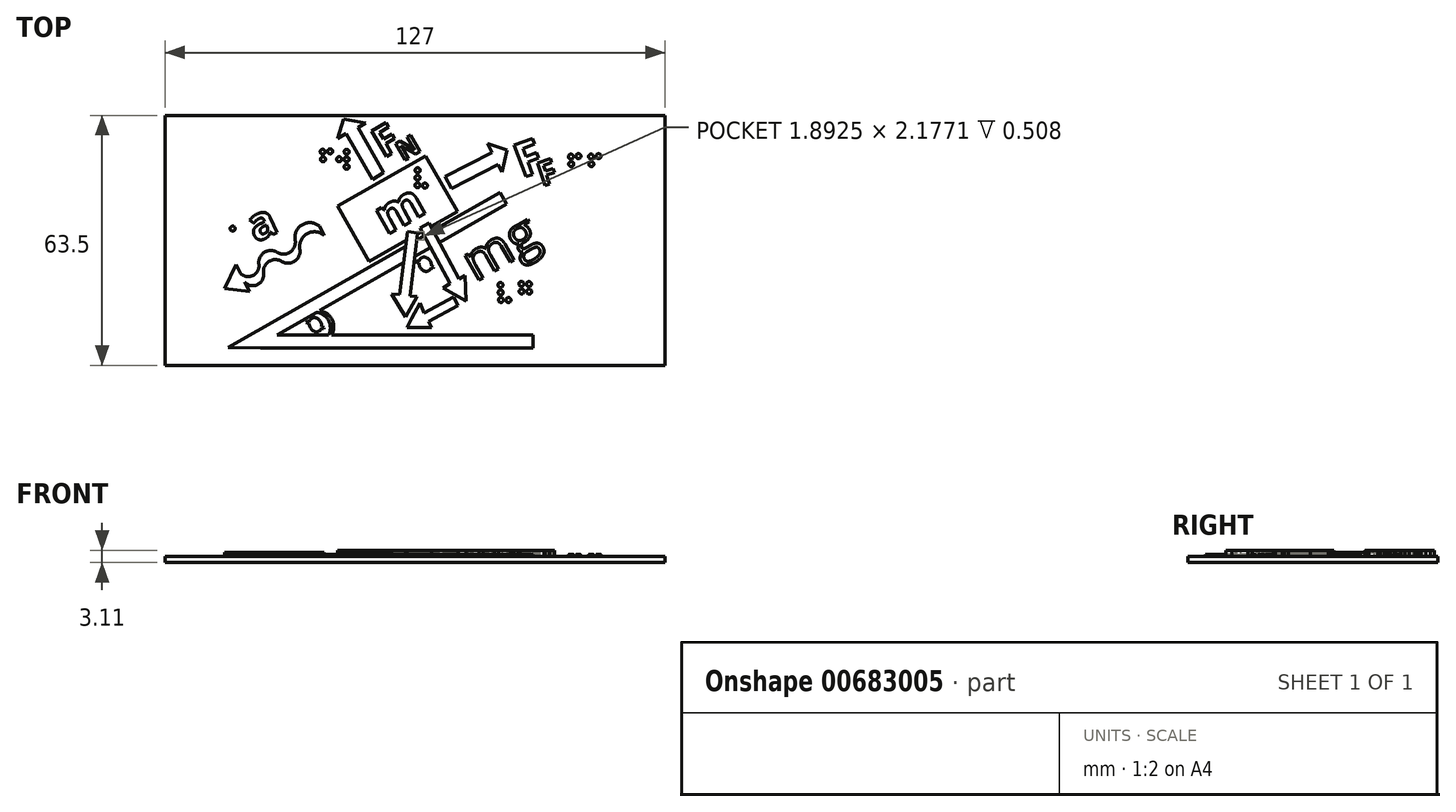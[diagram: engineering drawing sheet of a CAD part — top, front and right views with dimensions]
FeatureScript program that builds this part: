
annotation { "Feature Type Name" : "Feature", "Feature Type Description" : "" }
export const myFeature = defineFeature(function(context is Context, id is Id, definition is map)
    precondition{}
    {
        {
            var Q0;
            Q0=qCreatedBy(makeId("Top.planeOp"),FACE);
            var sketch = newSketch(context, id + "F0", { "sketchPlane" : qUnion([Q0])});
            skLineSegment(sketch, "E0.bottom", {"start": v(0, 0) * mm, "end": v(127, 0) * mm});
            skLineSegment(sketch, "E0.top", {"start": v(0, 63.5) * mm, "end": v(127, 63.5) * mm});
            skLineSegment(sketch, "E0.left", {"start": v(0, 0) * mm, "end": v(0, 63.5) * mm});
            skLineSegment(sketch, "E0.right", {"start": v(127, 0) * mm, "end": v(127, 63.5) * mm});
            skSolve(sketch);
        }
        {
            var Q0;
            Q0=makeQuery(id+"F0.imprint","IMPRINT",FACE,{"disambiguationData":[TD([[makeQuery(id+"F0.imprint","IMPRINT",EDGE,{"derivedFrom":sQuery(id+"F0.wireOp",EDGE,"E0.bottom")}),1.0]])]});
            extrude(context, id + "F1", {"entities" : qUnion([Q0]), "depth" : 1.59 * mm, "offsetDistance" : 25.4 * mm});
        }
        {
            var Q0;
            {var subQ0=sQuery(id+"F0.wireOp",EDGE,"E0.left");var subQ2=sQuery(id+"F0.wireOp",EDGE,"E0.top");var subQ4=sQuery(id+"F0.wireOp",EDGE,"E0.bottom");var subQ5=makeQuery(id+"F1.opExtrude","SWEPT_FACE",FACE,{"disambiguationData":[OSD([subQ4])]});var subQ9=sQuery(id+"F0.wireOp",EDGE,"E0.right");Q0=makeQuery(id+"F7.boolean.opBoolean","SPLIT",FACE,{"disambiguationData":[TD([subQ5])],"derivedFrom":makeQuery(id+"F5.boolean.opBoolean","SPLIT",FACE,{"disambiguationData":[TD([subQ5])],"derivedFrom":makeQuery(id+"F1.opExtrude","CAP_FACE",FACE,{"disambiguationData":[OSD([subQ4,subQ2,subQ0,subQ9])],"isStart":false})})});}
            var sketch = newSketch(context, id + "F2", { "sketchPlane" : qUnion([Q0])});
            skLineSegment(sketch, "E1", {"start": v(52.68, 47.22) * mm, "end": v(46.03, 58.88) * mm});
            skLineSegment(sketch, "E2", {"start": v(46.03, 58.88) * mm, "end": v(43.83, 57.63) * mm});
            skLineSegment(sketch, "E3", {"start": v(50.93, 61.6) * mm, "end": v(49.03, 60.45) * mm});
            skLineSegment(sketch, "E4", {"start": v(49.03, 60.45) * mm, "end": v(55.56, 48.98) * mm});
            skLineSegment(sketch, "E5", {"start": v(55.56, 48.98) * mm, "end": v(52.68, 47.22) * mm});
            skLineSegment(sketch, "E6", {"start": v(45.31, 62.57) * mm, "end": v(50.93, 61.6) * mm});
            skLineSegment(sketch, "E7", {"start": v(43.83, 57.63) * mm, "end": v(45.31, 62.57) * mm});
            skLineSegment(sketch, "E8", {"start": v(71.2, 47.9) * mm, "end": v(83.12, 54.07) * mm});
            skLineSegment(sketch, "E9", {"start": v(83.12, 54.07) * mm, "end": v(81.96, 56.33) * mm});
            skLineSegment(sketch, "E10", {"start": v(85.63, 49.07) * mm, "end": v(84.56, 51.01) * mm});
            skLineSegment(sketch, "E11", {"start": v(84.56, 51.01) * mm, "end": v(72.84, 44.95) * mm});
            skLineSegment(sketch, "E12", {"start": v(72.84, 44.95) * mm, "end": v(71.2, 47.9) * mm});
            skLineSegment(sketch, "E13", {"start": v(86.83, 54.64) * mm, "end": v(85.63, 49.07) * mm});
            skLineSegment(sketch, "E14", {"start": v(81.96, 56.33) * mm, "end": v(86.83, 54.64) * mm});
            skLineSegment(sketch, "E15", {"start": v(67.09, 36.17) * mm, "end": v(74.65, 21.92) * mm});
            skLineSegment(sketch, "E16", {"start": v(74.65, 21.92) * mm, "end": v(76.24, 22.77) * mm});
            skLineSegment(sketch, "E17", {"start": v(70.64, 19.62) * mm, "end": v(72.34, 20.73) * mm});
            skLineSegment(sketch, "E18", {"start": v(72.34, 20.73) * mm, "end": v(64.79, 34.9) * mm});
            skLineSegment(sketch, "E19", {"start": v(64.79, 34.9) * mm, "end": v(67.09, 36.17) * mm});
            skLineSegment(sketch, "E20", {"start": v(76.43, 16.38) * mm, "end": v(70.64, 19.62) * mm});
            skLineSegment(sketch, "E21", {"start": v(76.24, 22.77) * mm, "end": v(76.43, 16.38) * mm});
            skLineSegment(sketch, "E22", {"start": v(64.19, 33.65) * mm, "end": v(62.2, 17.65) * mm});
            skLineSegment(sketch, "E23", {"start": v(62.2, 17.65) * mm, "end": v(64, 17.42) * mm});
            skLineSegment(sketch, "E24", {"start": v(57.6, 18.06) * mm, "end": v(59.64, 17.99) * mm});
            skLineSegment(sketch, "E25", {"start": v(59.64, 17.99) * mm, "end": v(61.57, 33.93) * mm});
            skLineSegment(sketch, "E26", {"start": v(61.57, 33.93) * mm, "end": v(64.19, 33.65) * mm});
            skLineSegment(sketch, "E27", {"start": v(61.17, 12.24) * mm, "end": v(57.6, 18.06) * mm});
            skLineSegment(sketch, "E28", {"start": v(64, 17.42) * mm, "end": v(61.17, 12.24) * mm});
            skLineSegment(sketch, "E29", {"start": v(62.59, 11.93) * mm, "end": v(64.74, 15.88) * mm});
            skPoint(sketch, "E29.startSnap0", {"position": v(62.59, 14.83) * mm});
            skLineSegment(sketch, "E30", {"start": v(64.74, 15.88) * mm, "end": v(65.77, 13.33) * mm});
            skLineSegment(sketch, "E31", {"start": v(65.77, 13.33) * mm, "end": v(73.24, 17.35) * mm});
            skLineSegment(sketch, "E32", {"start": v(73.24, 17.35) * mm, "end": v(74.41, 15.16) * mm});
            skLineSegment(sketch, "E33", {"start": v(74.41, 15.16) * mm, "end": v(66.91, 11.12) * mm});
            skLineSegment(sketch, "E34", {"start": v(66.91, 11.12) * mm, "end": v(67.7, 9.65) * mm});
            skLineSegment(sketch, "E35", {"start": v(67.7, 9.65) * mm, "end": v(61.5, 9.65) * mm});
            skLineSegment(sketch, "E36", {"start": v(61.5, 9.65) * mm, "end": v(62.59, 11.93) * mm});
            skText(sketch, "E37", { "text": "F", "fontName": "OpenSans-Bold.ttf"});
            skText(sketch, "E38", { "text": "N", "fontName": "OpenSans-Bold.ttf"});
            skText(sketch, "E39", { "text": "F", "fontName": "OpenSans-Bold.ttf"});
            skText(sketch, "E40", { "text": "F", "fontName": "OpenSans-Bold.ttf"});
            skText(sketch, "E41", { "text": "mg", "fontName": "OpenSans-Regular.ttf"});
            skEllipticalArc(sketch, "E42", {});
            skFitSpline(sketch, "E43.0", {"points": [v(65.8, 27.08) * mm, v(65.41, 27) * mm, v(65.12, 26.74) * mm, v(64.93, 26.3) * mm, v(64.92, 25.75) * mm, v(65.1, 25.16) * mm, v(65.47, 24.67) * mm, v(65.93, 24.35) * mm, v(66.4, 24.25) * mm, v(66.77, 24.35) * mm, v(67.07, 24.6) * mm, v(67.26, 25.03) * mm, v(67.27, 25.6) * mm, v(67.08, 26.18) * mm, v(66.72, 26.67) * mm, v(66.25, 26.99) * mm, v(65.8, 27.08) * mm, v(65.41, 27) * mm, v(65.12, 26.74) * mm]});
            skLineSegment(sketch, "E44", {"start": v(63.77, 26.22) * mm, "end": v(64.5, 25.95) * mm});
            skLineSegment(sketch, "E45", {"start": v(68.11, 24.62) * mm, "end": v(68.25, 24.98) * mm});
            skLineSegment(sketch, "E46", {"start": v(68.25, 24.98) * mm, "end": v(67.68, 25.19) * mm});
            skLineSegment(sketch, "E47", {"start": v(63.94, 26.56) * mm, "end": v(63.77, 26.22) * mm});
            skFitSpline(sketch, "E48.trimOffspring", {"points": [v(65.8, 27.08) * mm, v(65.41, 27) * mm, v(65.12, 26.74) * mm, v(64.93, 26.3) * mm, v(64.92, 25.75) * mm, v(65.1, 25.16) * mm, v(65.47, 24.67) * mm, v(65.93, 24.35) * mm, v(66.4, 24.25) * mm, v(66.77, 24.35) * mm, v(67.07, 24.6) * mm, v(67.26, 25.03) * mm, v(67.27, 25.6) * mm, v(67.08, 26.18) * mm, v(66.72, 26.67) * mm, v(66.25, 26.99) * mm, v(65.8, 27.08) * mm, v(65.41, 27) * mm, v(65.12, 26.74) * mm]});
            skEllipticalArc(sketch, "E49.trimOffspring", {});
            skLineSegment(sketch, "E50.trimOffspring", {"start": v(67.61, 24.8) * mm, "end": v(68.11, 24.62) * mm});
            skLineSegment(sketch, "E51.trimOffspring", {"start": v(67.26, 25.34) * mm, "end": v(64.94, 26.2) * mm});
            skLineSegment(sketch, "E52.trimOffspring", {"start": v(64.53, 26.35) * mm, "end": v(63.94, 26.56) * mm});
            skLineSegment(sketch, "E53", {"start": v(64.94, 25.79) * mm, "end": v(67.2, 24.96) * mm});
            const initialGuessF2  = {"E37": [0.05542, 0.05258, 0.86603, 0.5, 0.0075], "E38": [0.0605, 0.05183, 0.86603, 0.5, 0.00486], "E39": [0.09064, 0.04753, 0.9397, 0.34202, 0.0086], "E40": [0.09575, 0.04539, 0.9518, 0.30672, 0.00612], "E41": [0.07882, 0.0211, 0.86603, 0.5, 0.00963], "E42": [0.06609338407474807, 0.025668868562019675, -0.4576420160499878, 0.8891365390904272, 0.0018890030002759763, 0.0015080474726828794, 1.0254476963977666, 3.8274184167815006], "E49.trimOffspring": [0.06609338407474807, 0.025668868562019675, -0.4576420160499878, 0.8891365390904272, 0.0018890030002759763, 0.0015080474726828794, 4.0541978294457675, 0.7986682837335095]};
            skSetInitialGuess(sketch, initialGuessF2);
            skSolve(sketch);
        }
        {
            var Q0;
            Q0=makeQuery(id+"F2.imprint","IMPRINT",FACE,{"disambiguationData":[TD([[makeQuery(id+"F2.imprint","IMPRINT",EDGE,{"derivedFrom":sQuery(id+"F2.wireOp",EDGE,"E37.sketch_text.stroke-0")}),-1.0]])]});
            var Q1;
            Q1=makeQuery(id+"F2.imprint","IMPRINT",FACE,{"disambiguationData":[TD([[makeQuery(id+"F2.imprint","IMPRINT",EDGE,{"derivedFrom":sQuery(id+"F2.wireOp",EDGE,"E38.sketch_text.stroke-0")}),-1.0]])]});
            var Q2;
            Q2=makeQuery(id+"F2.imprint","IMPRINT",FACE,{"disambiguationData":[TD([[makeQuery(id+"F2.imprint","IMPRINT",EDGE,{"derivedFrom":sQuery(id+"F2.wireOp",EDGE,"E39.sketch_text.stroke-0")}),-1.0]])]});
            var Q3;
            Q3=makeQuery(id+"F2.imprint","IMPRINT",FACE,{"disambiguationData":[TD([[makeQuery(id+"F2.imprint","IMPRINT",EDGE,{"derivedFrom":sQuery(id+"F2.wireOp",EDGE,"E40.sketch_text.stroke-0")}),-1.0]])]});
            var Q4;
            Q4=makeQuery(id+"F2.imprint","IMPRINT",FACE,{"disambiguationData":[TD([[makeQuery(id+"F2.imprint","IMPRINT",EDGE,{"derivedFrom":sQuery(id+"F2.wireOp",EDGE,"E41.sketch_text.stroke-28")}),-1.0]])]});
            var Q5;
            Q5=makeQuery(id+"F2.imprint","IMPRINT",FACE,{"disambiguationData":[TD([[makeQuery(id+"F2.imprint","IMPRINT",EDGE,{"derivedFrom":sQuery(id+"F2.wireOp",EDGE,"E41.sketch_text.stroke-0")}),-1.0]])]});
            var Q6;
            Q6=makeQuery(id+"F2.imprint","IMPRINT",FACE,{"disambiguationData":[TD([[makeQuery(id+"F2.imprint","IMPRINT",EDGE,{"derivedFrom":sQuery(id+"F2.wireOp",EDGE,"E42")}),1.0]])]});
            var Q7;
            {var subQ6=sQuery(id+"F2.wireOp",EDGE,"E23");Q7=makeQuery(id+"F2.imprint","IMPRINT",FACE,{"disambiguationData":[TD([[makeQuery(id+"F2.imprint","IMPRINT",EDGE,{"derivedFrom":subQ6}),-1.0]])]});}
            var Q8;
            Q8=makeQuery(id+"F2.imprint","IMPRINT",FACE,{"disambiguationData":[TD([[makeQuery(id+"F2.imprint","IMPRINT",EDGE,{"derivedFrom":sQuery(id+"F2.wireOp",EDGE,"E29")}),-1.0]])]});
            var Q9;
            {var subQ6=sQuery(id+"F2.wireOp",EDGE,"E16");Q9=makeQuery(id+"F2.imprint","IMPRINT",FACE,{"disambiguationData":[TD([[makeQuery(id+"F2.imprint","IMPRINT",EDGE,{"derivedFrom":subQ6}),-1.0]])]});}
            var Q10;
            {var subQ0=sQuery(id+"F2.wireOp",EDGE,"E22");var subQ1=makeQuery(id+"F7.opExtrude","CAP_EDGE",EDGE,{"disambiguationData":[OSD([sQuery(id+"F6.wireOp",EDGE,"E80")])],"isStart":true});var subQ2=makeQuery(id+"F2.imprint","INTERSECT",VERTEX,{"derivedFrom":[subQ1,subQ0]});Q10=makeQuery(id+"F2.imprint","IMPRINT",FACE,{"disambiguationData":[TD([[makeQuery(id+"F2.imprint","IMPRINT",EDGE,{"disambiguationData":[TD([[subQ2,-1.0]])],"derivedFrom":subQ0}),-1.0]])]});}
            var Q11;
            {var subQ0=sQuery(id+"F2.wireOp",EDGE,"E15");var subQ1=makeQuery(id+"F7.opExtrude","CAP_EDGE",EDGE,{"disambiguationData":[OSD([sQuery(id+"F6.wireOp",EDGE,"E80")])],"isStart":true});var subQ2=makeQuery(id+"F2.imprint","INTERSECT",VERTEX,{"derivedFrom":[subQ1,subQ0]});Q11=makeQuery(id+"F2.imprint","IMPRINT",FACE,{"disambiguationData":[TD([[makeQuery(id+"F2.imprint","IMPRINT",EDGE,{"disambiguationData":[TD([[subQ2,-1.0]])],"derivedFrom":subQ0}),-1.0]])]});}
            var Q12;
            Q12=makeQuery(id+"F2.imprint","IMPRINT",FACE,{"disambiguationData":[TD([[makeQuery(id+"F2.imprint","IMPRINT",EDGE,{"derivedFrom":sQuery(id+"F2.wireOp",EDGE,"E8")}),-1.0]])]});
            var Q13;
            Q13=makeQuery(id+"F2.imprint","IMPRINT",FACE,{"disambiguationData":[TD([[makeQuery(id+"F2.imprint","IMPRINT",EDGE,{"derivedFrom":sQuery(id+"F2.wireOp",EDGE,"E1")}),-1.0]])]});
            extrude(context, id + "F3", {"entities" : qUnion([Q0, Q1, Q2, Q3, Q4, Q5, Q6, Q7, Q8, Q9, Q10, Q11, Q12, Q13]), "operationType" : NewBodyOperationType.ADD, "depth" : 1.52 * mm, "offsetDistance" : 25.4 * mm});
        }
        {
            var Q0;
            Q0=makeQuery(id+"F1.opExtrude","CAP_FACE",FACE,{"disambiguationData":[OSD([sQuery(id+"F0.wireOp",EDGE,"E0.bottom"),sQuery(id+"F0.wireOp",EDGE,"E0.top"),sQuery(id+"F0.wireOp",EDGE,"E0.left"),sQuery(id+"F0.wireOp",EDGE,"E0.right")])],"isStart":false});
            var sketch = newSketch(context, id + "F4", { "sketchPlane" : qUnion([Q0])});
            skLineSegment(sketch, "E54", {"start": v(24.26, 4.4) * mm, "end": v(93.55, 4.4) * mm});
            skLineSegment(sketch, "E55", {"start": v(93.55, 4.4) * mm, "end": v(93.55, 7.72) * mm});
            skLineSegment(sketch, "E56", {"start": v(93.55, 7.72) * mm, "end": v(42.34, 7.72) * mm});
            skLineSegment(sketch, "E57", {"start": v(28.42, 7.72) * mm, "end": v(38.48, 13.46) * mm});
            skLineSegment(sketch, "E58", {"start": v(86.74, 40.95) * mm, "end": v(85.09, 43.85) * mm});
            skLineSegment(sketch, "E59", {"start": v(85.09, 43.85) * mm, "end": v(16.03, 4.5) * mm});
            skLineSegment(sketch, "E60", {"start": v(16.03, 4.5) * mm, "end": v(24.26, 4.4) * mm});
            skArc(sketch, "E61", {"start": v(41.55, 7.72) * mm, "mid": v(41.53, 11.4) * mm, "end": v(38.48, 13.46) * mm});
            skArc(sketch, "E62", {"start": v(42.34, 7.72) * mm, "mid": v(42.43, 11.63) * mm, "end": v(39.24, 13.89) * mm});
            skLineSegment(sketch, "E63.trimOffspring", {"start": v(39.24, 13.89) * mm, "end": v(86.74, 40.95) * mm});
            skLineSegment(sketch, "E64.trimOffspring", {"start": v(41.55, 7.72) * mm, "end": v(28.42, 7.72) * mm});
            skEllipticalArc(sketch, "E65", {});
            skFitSpline(sketch, "E66.0", {"points": [v(37.92, 11.73) * mm, v(37.54, 11.64) * mm, v(37.24, 11.39) * mm, v(37.05, 10.96) * mm, v(37.04, 10.4) * mm, v(37.23, 9.81) * mm, v(37.6, 9.32) * mm, v(38.06, 9) * mm, v(38.52, 8.9) * mm, v(38.9, 9) * mm, v(39.2, 9.25) * mm, v(39.38, 9.68) * mm, v(39.4, 10.24) * mm, v(39.2, 10.83) * mm, v(38.84, 11.32) * mm, v(38.38, 11.64) * mm, v(37.92, 11.73) * mm, v(37.54, 11.64) * mm, v(37.24, 11.39) * mm]});
            skLineSegment(sketch, "E67", {"start": v(35.9, 10.87) * mm, "end": v(36.62, 10.6) * mm});
            skLineSegment(sketch, "E68", {"start": v(40.24, 9.27) * mm, "end": v(40.37, 9.63) * mm});
            skLineSegment(sketch, "E69", {"start": v(40.37, 9.63) * mm, "end": v(39.8, 9.84) * mm});
            skLineSegment(sketch, "E70", {"start": v(36.06, 11.21) * mm, "end": v(35.9, 10.87) * mm});
            skFitSpline(sketch, "E71.trimOffspring", {"points": [v(37.92, 11.73) * mm, v(37.54, 11.64) * mm, v(37.24, 11.39) * mm, v(37.05, 10.96) * mm, v(37.04, 10.4) * mm, v(37.23, 9.81) * mm, v(37.6, 9.32) * mm, v(38.06, 9) * mm, v(38.52, 8.9) * mm, v(38.9, 9) * mm, v(39.2, 9.25) * mm, v(39.38, 9.68) * mm, v(39.4, 10.24) * mm, v(39.2, 10.83) * mm, v(38.84, 11.32) * mm, v(38.38, 11.64) * mm, v(37.92, 11.73) * mm, v(37.54, 11.64) * mm, v(37.24, 11.39) * mm]});
            skEllipticalArc(sketch, "E72.trimOffspring", {});
            skLineSegment(sketch, "E73.trimOffspring", {"start": v(39.74, 9.46) * mm, "end": v(40.24, 9.27) * mm});
            skLineSegment(sketch, "E74.trimOffspring", {"start": v(39.38, 10) * mm, "end": v(37.07, 10.84) * mm});
            skLineSegment(sketch, "E75.trimOffspring", {"start": v(36.65, 11) * mm, "end": v(36.06, 11.21) * mm});
            skLineSegment(sketch, "E76", {"start": v(37.07, 10.44) * mm, "end": v(39.33, 9.6) * mm});
            const initialGuessF4  = {"E65": [0.038218526944156374, 0.010319110858641223, -0.4576420160499878, 0.8891365390904272, 0.0018890030002759763, 0.0015080474726828794, 1.0254476963977666, 3.827418836985673], "E72.trimOffspring": [0.038218526944156374, 0.010319110858641223, -0.4576420160499878, 0.8891365390904272, 0.0018890030002759763, 0.0015080474726828794, 4.0541978294457675, 0.7986687039376736]};
            skSetInitialGuess(sketch, initialGuessF4);
            skSolve(sketch);
        }
        {
            var Q0;
            Q0=makeQuery(id+"F4.imprint","IMPRINT",FACE,{"disambiguationData":[TD([[makeQuery(id+"F4.imprint","IMPRINT",EDGE,{"derivedFrom":sQuery(id+"F4.wireOp",EDGE,"E54")}),1.0]])]});
            var Q1;
            Q1=makeQuery(id+"F4.imprint","IMPRINT",FACE,{"disambiguationData":[TD([[makeQuery(id+"F4.imprint","IMPRINT",EDGE,{"derivedFrom":sQuery(id+"F4.wireOp",EDGE,"E65")}),1.0]])]});
            var Q2;
            {var subQ0=sQuery(id+"F4.wireOp",EDGE,"E59");var subQ1=makeQuery(id+"F3.opExtrude","CAP_EDGE",EDGE,{"disambiguationData":[OSD([sQuery(id+"F2.wireOp",EDGE,"E18")])],"isStart":true});var subQ2=makeQuery(id+"F4.imprint","INTERSECT",VERTEX,{"derivedFrom":[subQ1,subQ0]});Q2=makeQuery(id+"F4.imprint","IMPRINT",FACE,{"disambiguationData":[TD([[makeQuery(id+"F4.imprint","IMPRINT",EDGE,{"disambiguationData":[TD([[subQ2,-1.0]])],"derivedFrom":subQ0}),1.0]])]});}
            var Q3;
            {var subQ0=sQuery(id+"F4.wireOp",EDGE,"E58");Q3=makeQuery(id+"F4.imprint","IMPRINT",FACE,{"disambiguationData":[TD([[makeQuery(id+"F4.imprint","IMPRINT",EDGE,{"derivedFrom":subQ0}),1.0]])]});}
            extrude(context, id + "F5", {"entities" : qUnion([Q0, Q1, Q2, Q3]), "operationType" : NewBodyOperationType.ADD, "depth" : 0.5 * mm, "offsetDistance" : 25.4 * mm});
        }
        {
            var Q0;
            {var subQ0=sQuery(id+"F0.wireOp",EDGE,"E0.left");var subQ1=sQuery(id+"F0.wireOp",EDGE,"E0.bottom");var subQ2=sQuery(id+"F0.wireOp",EDGE,"E0.right");var subQ3=sQuery(id+"F0.wireOp",EDGE,"E0.top");Q0=makeQuery(id+"F5.boolean.opBoolean","SPLIT",FACE,{"disambiguationData":[TD([makeQuery(id+"F1.opExtrude","SWEPT_FACE",FACE,{"disambiguationData":[OSD([subQ1])]})])],"derivedFrom":makeQuery(id+"F1.opExtrude","CAP_FACE",FACE,{"disambiguationData":[OSD([subQ1,subQ3,subQ0,subQ2])],"isStart":false})});}
            var sketch = newSketch(context, id + "F6", { "sketchPlane" : qUnion([Q0])});
            skLineSegment(sketch, "E77", {"start": v(51.82, 26.43) * mm, "end": v(43.83, 40.46) * mm});
            skLineSegment(sketch, "E78", {"start": v(43.83, 40.46) * mm, "end": v(66.23, 53.22) * mm});
            skLineSegment(sketch, "E79", {"start": v(66.23, 53.22) * mm, "end": v(74.3, 39.07) * mm});
            skLineSegment(sketch, "E80", {"start": v(74.3, 39.07) * mm, "end": v(51.82, 26.43) * mm});
            skText(sketch, "E81", { "text": "m", "fontName": "OpenSans-Bold.ttf"});
            skArc(sketch, "E82", {"start": v(40.42, 33.04) * mm, "mid": v(36.2, 33.5) * mm, "end": v(34.18, 29.79) * mm});
            skArc(sketch, "E83", {"start": v(29.81, 26.29) * mm, "mid": v(33.15, 26.6) * mm, "end": v(34.18, 29.79) * mm});
            skArc(sketch, "E84", {"start": v(29.81, 26.29) * mm, "mid": v(26.5, 26.44) * mm, "end": v(25, 23.49) * mm});
            skArc(sketch, "E85", {"start": v(20.18, 21.16) * mm, "mid": v(23.47, 20.5) * mm, "end": v(25, 23.49) * mm});
            skArc(sketch, "E86", {"start": v(39.23, 35.35) * mm, "mid": v(35.02, 35.82) * mm, "end": v(33, 32.1) * mm});
            skArc(sketch, "E87", {"start": v(28.63, 28.6) * mm, "mid": v(31.96, 28.91) * mm, "end": v(33, 32.1) * mm});
            skArc(sketch, "E88", {"start": v(28.63, 28.6) * mm, "mid": v(25.32, 28.75) * mm, "end": v(23.82, 25.8) * mm});
            skArc(sketch, "E89", {"start": v(19.19, 23.27) * mm, "mid": v(22.41, 22.87) * mm, "end": v(23.82, 25.8) * mm});
            skLineSegment(sketch, "E90", {"start": v(39.23, 35.35) * mm, "end": v(40.42, 33.04) * mm});
            skLineSegment(sketch, "E91", {"start": v(20.18, 21.16) * mm, "end": v(21.48, 18.77) * mm});
            skLineSegment(sketch, "E92", {"start": v(21.48, 18.77) * mm, "end": v(15.08, 19.55) * mm});
            skLineSegment(sketch, "E93", {"start": v(15.08, 19.55) * mm, "end": v(18.1, 25.57) * mm});
            skLineSegment(sketch, "E94", {"start": v(18.1, 25.57) * mm, "end": v(19.19, 23.27) * mm});
            skText(sketch, "E95", { "text": "a", "fontName": "OpenSans-Bold.ttf"});
            const initialGuessF6  = {"E81": [0.05625, 0.033, 0.87092, 0.49143, 0.00893], "E95": [0.023, 0.03117, 0.9063, 0.42262, 0.00829]};
            skSetInitialGuess(sketch, initialGuessF6);
            skSolve(sketch);
        }
        {
            var Q0;
            Q0=makeQuery(id+"F6.imprint","IMPRINT",FACE,{"disambiguationData":[TD([[makeQuery(id+"F6.imprint","IMPRINT",EDGE,{"derivedFrom":sQuery(id+"F6.wireOp",EDGE,"E82")}),-1.0]])]});
            var Q1;
            Q1=makeQuery(id+"F6.imprint","IMPRINT",FACE,{"disambiguationData":[TD([[makeQuery(id+"F6.imprint","IMPRINT",EDGE,{"derivedFrom":sQuery(id+"F6.wireOp",EDGE,"E95.sketch_text.stroke-0")}),-1.0]])]});
            var Q2;
            Q2=makeQuery(id+"F6.imprint","IMPRINT",FACE,{"disambiguationData":[TD([[makeQuery(id+"F6.imprint","IMPRINT",EDGE,{"derivedFrom":sQuery(id+"F6.wireOp",EDGE,"E77")}),-1.0]])]});
            extrude(context, id + "F7", {"entities" : qUnion([Q0, Q1, Q2]), "operationType" : NewBodyOperationType.ADD, "depth" : 1.02 * mm, "offsetDistance" : 25.4 * mm});
        }
        {
            var Q0;
            {var subQ19=sQuery(id+"F0.wireOp",EDGE,"E0.right");var subQ20=sQuery(id+"F0.wireOp",EDGE,"E0.left");var subQ21=sQuery(id+"F0.wireOp",EDGE,"E0.top");var subQ22=sQuery(id+"F0.wireOp",EDGE,"E0.bottom");var subQ23=makeQuery(id+"F1.opExtrude","CAP_FACE",FACE,{"disambiguationData":[OSD([subQ22,subQ21,subQ20,subQ19])],"isStart":false});var subQ86=makeQuery(id+"F1.opExtrude","SWEPT_FACE",FACE,{"disambiguationData":[OSD([subQ22])]});Q0=makeQuery(id+"F7.boolean.opBoolean","SPLIT",FACE,{"disambiguationData":[TD([subQ86])],"derivedFrom":makeQuery(id+"F5.boolean.opBoolean","SPLIT",FACE,{"disambiguationData":[TD([subQ86])],"derivedFrom":makeQuery(id+"F3.boolean.opBoolean","SPLIT",FACE,{"disambiguationData":[TD([subQ86])],"derivedFrom":subQ23})})});}
            var sketch = newSketch(context, id + "F8", { "sketchPlane" : qUnion([Q0])});
            skCircle(sketch, "E96", {"center": v(40.06, 54.25) * mm, "radius": 0.64 * mm});
            skCircle(sketch, "E97", {"center": v(41.96, 54.36) * mm, "radius": 0.64 * mm});
            skCircle(sketch, "E98", {"center": v(40.13, 52.34) * mm, "radius": 0.64 * mm});
            skCircle(sketch, "E99", {"center": v(44.23, 52.35) * mm, "radius": 0.64 * mm});
            skCircle(sketch, "E100", {"center": v(46.15, 54.24) * mm, "radius": 0.64 * mm});
            skCircle(sketch, "E101", {"center": v(46.13, 52.34) * mm, "radius": 0.64 * mm});
            skCircle(sketch, "E102", {"center": v(46.14, 50.43) * mm, "radius": 0.64 * mm});
            skCircle(sketch, "E103", {"center": v(103.13, 53.02) * mm, "radius": 0.64 * mm});
            skCircle(sketch, "E104", {"center": v(105.03, 53.14) * mm, "radius": 0.64 * mm});
            skCircle(sketch, "E105", {"center": v(103.2, 51.12) * mm, "radius": 0.64 * mm});
            skCircle(sketch, "E106", {"center": v(108.23, 53.03) * mm, "radius": 0.64 * mm});
            skCircle(sketch, "E107", {"center": v(110.13, 53.14) * mm, "radius": 0.64 * mm});
            skCircle(sketch, "E108", {"center": v(108.3, 51.12) * mm, "radius": 0.64 * mm});
            skCircle(sketch, "E109", {"center": v(85.22, 20.4) * mm, "radius": 0.64 * mm});
            skCircle(sketch, "E110", {"center": v(85.26, 18.5) * mm, "radius": 0.64 * mm});
            skCircle(sketch, "E111", {"center": v(85.34, 16.59) * mm, "radius": 0.64 * mm});
            skCircle(sketch, "E112", {"center": v(87.24, 16.58) * mm, "radius": 0.64 * mm});
            skCircle(sketch, "E113", {"center": v(90.55, 20.67) * mm, "radius": 0.64 * mm});
            skCircle(sketch, "E114", {"center": v(90.59, 18.76) * mm, "radius": 0.64 * mm});
            skCircle(sketch, "E115", {"center": v(92.45, 20.63) * mm, "radius": 0.64 * mm});
            skCircle(sketch, "E116", {"center": v(92.5, 18.72) * mm, "radius": 0.64 * mm});
            skCircle(sketch, "E117", {"center": v(17.17, 34.73) * mm, "radius": 0.64 * mm});
            skSolve(sketch);
        }
        {
            var Q0;
            Q0 = qSketchRegion(id + "F8", true);
            extrude(context, id + "F9", {"entities" : qUnion([Q0]), "operationType" : NewBodyOperationType.ADD, "depth" : 0.5 * mm, "offsetDistance" : 25.4 * mm});
        }
        {
            var Q0;
            Q0=makeQuery(id+"F9.opExtrude","CAP_EDGE",EDGE,{"disambiguationData":[OSD([sQuery(id+"F8.wireOp",EDGE,"E117")])],"isStart":false});
            var Q1;
            Q1=makeQuery(id+"F9.opExtrude","CAP_FACE",FACE,{"disambiguationData":[OSD([sQuery(id+"F8.wireOp",EDGE,"E98")])],"isStart":false});
            var Q2;
            Q2=makeQuery(id+"F9.opExtrude","CAP_EDGE",EDGE,{"disambiguationData":[OSD([sQuery(id+"F8.wireOp",EDGE,"E96")])],"isStart":false});
            var Q3;
            Q3=makeQuery(id+"F9.opExtrude","CAP_EDGE",EDGE,{"disambiguationData":[OSD([sQuery(id+"F8.wireOp",EDGE,"E97")])],"isStart":false});
            var Q4;
            Q4=makeQuery(id+"F9.opExtrude","CAP_EDGE",EDGE,{"disambiguationData":[OSD([sQuery(id+"F8.wireOp",EDGE,"E99")])],"isStart":false});
            var Q5;
            Q5=makeQuery(id+"F9.opExtrude","CAP_EDGE",EDGE,{"disambiguationData":[OSD([sQuery(id+"F8.wireOp",EDGE,"E101")])],"isStart":false});
            var Q6;
            Q6=makeQuery(id+"F9.opExtrude","CAP_EDGE",EDGE,{"disambiguationData":[OSD([sQuery(id+"F8.wireOp",EDGE,"E100")])],"isStart":false});
            var Q7;
            Q7=makeQuery(id+"F9.opExtrude","CAP_EDGE",EDGE,{"disambiguationData":[OSD([sQuery(id+"F8.wireOp",EDGE,"E102")])],"isStart":false});
            var Q8;
            Q8=makeQuery(id+"F9.opExtrude","CAP_EDGE",EDGE,{"disambiguationData":[OSD([sQuery(id+"F8.wireOp",EDGE,"E105")])],"isStart":false});
            var Q9;
            Q9=makeQuery(id+"F9.opExtrude","CAP_EDGE",EDGE,{"disambiguationData":[OSD([sQuery(id+"F8.wireOp",EDGE,"E103")])],"isStart":false});
            var Q10;
            Q10=makeQuery(id+"F9.opExtrude","CAP_EDGE",EDGE,{"disambiguationData":[OSD([sQuery(id+"F8.wireOp",EDGE,"E104")])],"isStart":false});
            var Q11;
            Q11=makeQuery(id+"F9.opExtrude","CAP_EDGE",EDGE,{"disambiguationData":[OSD([sQuery(id+"F8.wireOp",EDGE,"E106")])],"isStart":false});
            var Q12;
            Q12=makeQuery(id+"F9.opExtrude","CAP_EDGE",EDGE,{"disambiguationData":[OSD([sQuery(id+"F8.wireOp",EDGE,"E108")])],"isStart":false});
            var Q13;
            Q13=makeQuery(id+"F9.opExtrude","CAP_EDGE",EDGE,{"disambiguationData":[OSD([sQuery(id+"F8.wireOp",EDGE,"E107")])],"isStart":false});
            var Q14;
            Q14=makeQuery(id+"F9.opExtrude","CAP_EDGE",EDGE,{"disambiguationData":[OSD([sQuery(id+"F8.wireOp",EDGE,"E116")])],"isStart":false});
            var Q15;
            Q15=makeQuery(id+"F9.opExtrude","CAP_EDGE",EDGE,{"disambiguationData":[OSD([sQuery(id+"F8.wireOp",EDGE,"E115")])],"isStart":false});
            var Q16;
            Q16=makeQuery(id+"F9.opExtrude","CAP_EDGE",EDGE,{"disambiguationData":[OSD([sQuery(id+"F8.wireOp",EDGE,"E113")])],"isStart":false});
            var Q17;
            Q17=makeQuery(id+"F9.opExtrude","CAP_EDGE",EDGE,{"disambiguationData":[OSD([sQuery(id+"F8.wireOp",EDGE,"E114")])],"isStart":false});
            var Q18;
            Q18=makeQuery(id+"F9.opExtrude","CAP_EDGE",EDGE,{"disambiguationData":[OSD([sQuery(id+"F8.wireOp",EDGE,"E112")])],"isStart":false});
            var Q19;
            Q19=makeQuery(id+"F9.opExtrude","CAP_EDGE",EDGE,{"disambiguationData":[OSD([sQuery(id+"F8.wireOp",EDGE,"E111")])],"isStart":false});
            var Q20;
            Q20=makeQuery(id+"F9.opExtrude","CAP_EDGE",EDGE,{"disambiguationData":[OSD([sQuery(id+"F8.wireOp",EDGE,"E110")])],"isStart":false});
            var Q21;
            Q21=makeQuery(id+"F9.opExtrude","CAP_EDGE",EDGE,{"disambiguationData":[OSD([sQuery(id+"F8.wireOp",EDGE,"E109")])],"isStart":false});
            fillet(context, id + "F10", {"entities" : qUnion([Q0, Q1, Q2, Q3, Q4, Q5, Q6, Q7, Q8, Q9, Q10, Q11, Q12, Q13, Q14, Q15, Q16, Q17, Q18, Q19, Q20, Q21]), "radius" : 0.25 * mm, "tangentPropagation" : true, "allowEdgeOverflow" : false});
        }
        {
            var Q0;
            Q0=makeQuery(id+"F7.opExtrude","CAP_FACE",FACE,{"disambiguationData":[OSD([sQuery(id+"F2.wireOp",EDGE,"E15"),sQuery(id+"F2.wireOp",EDGE,"E18"),sQuery(id+"F2.wireOp",EDGE,"E19"),sQuery(id+"F2.wireOp",EDGE,"E22"),sQuery(id+"F2.wireOp",EDGE,"E25"),sQuery(id+"F2.wireOp",EDGE,"E26"),sQuery(id+"F6.wireOp",EDGE,"E77"),sQuery(id+"F6.wireOp",EDGE,"E78"),sQuery(id+"F6.wireOp",EDGE,"E79"),sQuery(id+"F6.wireOp",EDGE,"E80"),sQuery(id+"F6.wireOp",EDGE,"E81.sketch_text.stroke-0"),sQuery(id+"F6.wireOp",EDGE,"E81.sketch_text.stroke-1"),sQuery(id+"F6.wireOp",EDGE,"E81.sketch_text.stroke-2"),sQuery(id+"F6.wireOp",EDGE,"E81.sketch_text.stroke-3"),sQuery(id+"F6.wireOp",EDGE,"E81.sketch_text.stroke-4"),sQuery(id+"F6.wireOp",EDGE,"E81.sketch_text.stroke-5"),sQuery(id+"F6.wireOp",EDGE,"E81.sketch_text.stroke-6"),sQuery(id+"F6.wireOp",EDGE,"E81.sketch_text.stroke-7"),sQuery(id+"F6.wireOp",EDGE,"E81.sketch_text.stroke-8"),sQuery(id+"F6.wireOp",EDGE,"E81.sketch_text.stroke-9"),sQuery(id+"F6.wireOp",EDGE,"E81.sketch_text.stroke-10"),sQuery(id+"F6.wireOp",EDGE,"E81.sketch_text.stroke-11"),sQuery(id+"F6.wireOp",EDGE,"E81.sketch_text.stroke-12"),sQuery(id+"F6.wireOp",EDGE,"E81.sketch_text.stroke-13"),sQuery(id+"F6.wireOp",EDGE,"E81.sketch_text.stroke-14"),sQuery(id+"F6.wireOp",EDGE,"E81.sketch_text.stroke-15"),sQuery(id+"F6.wireOp",EDGE,"E81.sketch_text.stroke-16"),sQuery(id+"F6.wireOp",EDGE,"E81.sketch_text.stroke-17"),sQuery(id+"F6.wireOp",EDGE,"E81.sketch_text.stroke-18"),sQuery(id+"F6.wireOp",EDGE,"E81.sketch_text.stroke-19"),sQuery(id+"F6.wireOp",EDGE,"E81.sketch_text.stroke-20"),sQuery(id+"F6.wireOp",EDGE,"E81.sketch_text.stroke-21"),sQuery(id+"F6.wireOp",EDGE,"E81.sketch_text.stroke-22"),sQuery(id+"F6.wireOp",EDGE,"E81.sketch_text.stroke-23"),sQuery(id+"F6.wireOp",EDGE,"E81.sketch_text.stroke-24"),sQuery(id+"F6.wireOp",EDGE,"E81.sketch_text.stroke-25"),sQuery(id+"F6.wireOp",EDGE,"E81.sketch_text.stroke-26"),sQuery(id+"F6.wireOp",EDGE,"E81.sketch_text.stroke-27")])],"isStart":false});
            var sketch = newSketch(context, id + "F11", { "sketchPlane" : qUnion([Q0])});
            skCircle(sketch, "E118", {"center": v(64.17, 49.55) * mm, "radius": 0.64 * mm});
            skCircle(sketch, "E119", {"center": v(64.12, 47.64) * mm, "radius": 0.64 * mm});
            skCircle(sketch, "E120", {"center": v(64.12, 45.74) * mm, "radius": 0.64 * mm});
            skCircle(sketch, "E121", {"center": v(66.02, 45.64) * mm, "radius": 0.64 * mm});
            skSolve(sketch);
        }
        {
            var Q0;
            Q0=makeQuery(id+"F11.imprint","IMPRINT",FACE,{"disambiguationData":[TD([[makeQuery(id+"F11.imprint","IMPRINT",EDGE,{"derivedFrom":sQuery(id+"F11.wireOp",EDGE,"E118")}),1.0]])]});
            var Q1;
            Q1=makeQuery(id+"F11.imprint","IMPRINT",FACE,{"disambiguationData":[TD([[makeQuery(id+"F11.imprint","IMPRINT",EDGE,{"derivedFrom":sQuery(id+"F11.wireOp",EDGE,"E119")}),1.0]])]});
            var Q2;
            Q2=makeQuery(id+"F11.imprint","IMPRINT",FACE,{"disambiguationData":[TD([[makeQuery(id+"F11.imprint","IMPRINT",EDGE,{"derivedFrom":sQuery(id+"F11.wireOp",EDGE,"E120")}),1.0]])]});
            var Q3;
            Q3=makeQuery(id+"F11.imprint","IMPRINT",FACE,{"disambiguationData":[TD([[makeQuery(id+"F11.imprint","IMPRINT",EDGE,{"derivedFrom":sQuery(id+"F11.wireOp",EDGE,"E121")}),1.0]])]});
            extrude(context, id + "F12", {"entities" : qUnion([Q0, Q1, Q2, Q3]), "operationType" : NewBodyOperationType.ADD, "depth" : 0.5 * mm, "offsetDistance" : 25.4 * mm});
        }
        {
            var Q0;
            Q0=makeQuery(id+"F12.opExtrude","CAP_EDGE",EDGE,{"disambiguationData":[OSD([sQuery(id+"F11.wireOp",EDGE,"E118")])],"isStart":false});
            var Q1;
            Q1=makeQuery(id+"F12.opExtrude","CAP_EDGE",EDGE,{"disambiguationData":[OSD([sQuery(id+"F11.wireOp",EDGE,"E119")])],"isStart":false});
            var Q2;
            Q2=makeQuery(id+"F12.opExtrude","CAP_EDGE",EDGE,{"disambiguationData":[OSD([sQuery(id+"F11.wireOp",EDGE,"E120")])],"isStart":false});
            var Q3;
            Q3=makeQuery(id+"F12.opExtrude","CAP_EDGE",EDGE,{"disambiguationData":[OSD([sQuery(id+"F11.wireOp",EDGE,"E121")])],"isStart":false});
            fillet(context, id + "F13", {"entities" : qUnion([Q0, Q1, Q2, Q3]), "radius" : 0.25 * mm, "tangentPropagation" : true, "allowEdgeOverflow" : false});
        }
    });
